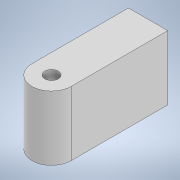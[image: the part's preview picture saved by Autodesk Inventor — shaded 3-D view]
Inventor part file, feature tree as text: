
AUTODESK INVENTOR PART (.ipt)
format: ipt  version: 2022 (Build 260153000, 153)  size: 93,696 bytes
history: native  units: mm
features: extrude x1, sketch x1
ambient origin geometry x8: Origin, YZ Plane, XZ Plane, XY Plane, X Axis, Y Axis, Z Axis, Center Point
bodies: Solid1 (feature_tree)
feature tree (2):
  extrude  "Extrusion1"  Depth=10.0mm
  sketch  "Sketch1"  dims[d0=2.1mm d1=2.0mm d2=15.0mm d3=10.0mm d4=0.0mm]
